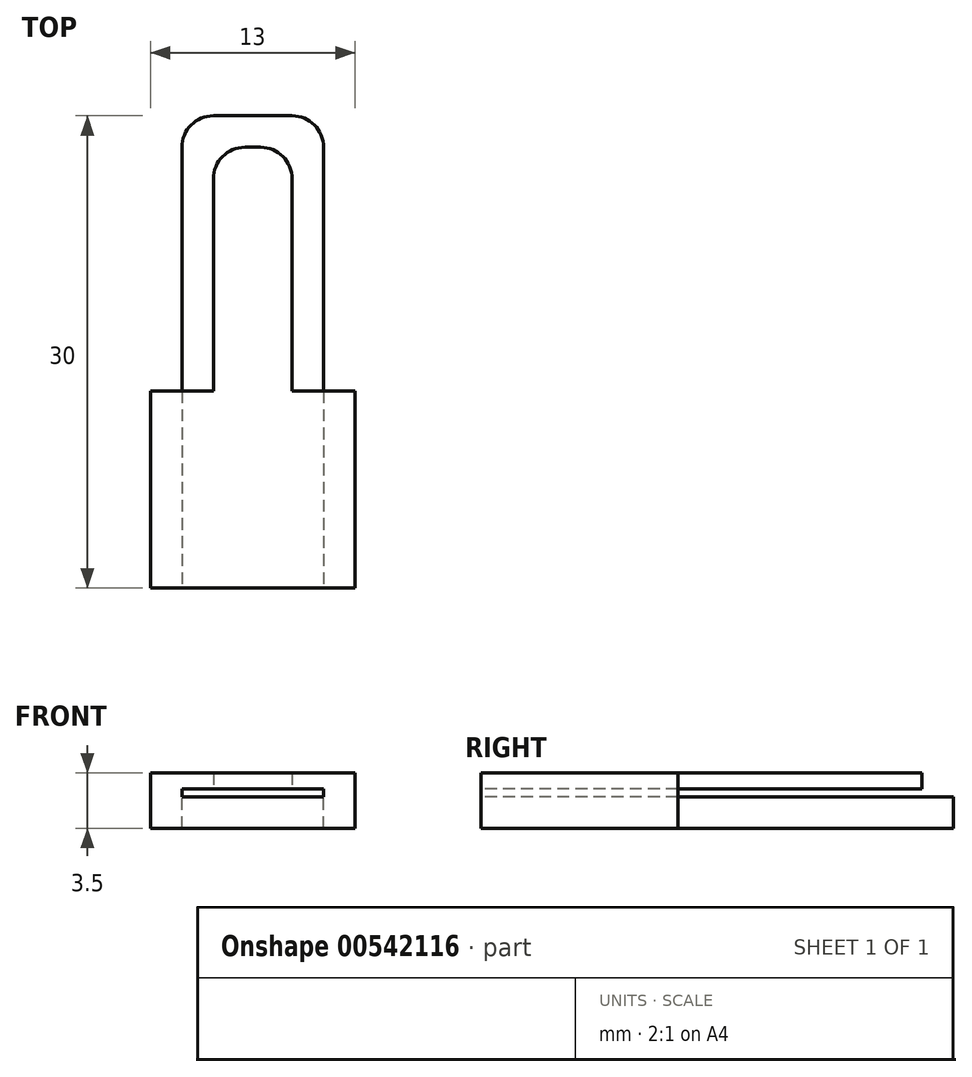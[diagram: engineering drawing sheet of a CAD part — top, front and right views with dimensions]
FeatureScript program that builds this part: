
annotation { "Feature Type Name" : "Feature", "Feature Type Description" : "" }
export const myFeature = defineFeature(function(context is Context, id is Id, definition is map)
    precondition{}
    {
        {
            var Q0;
            Q0=qCreatedBy(makeId("Top.planeOp"),FACE);
            var sketch = newSketch(context, id + "F0", { "sketchPlane" : qUnion([Q0])});
            skLineSegment(sketch, "E0.bottom", {"start": v(4.5, 15) * mm, "end": v(-4.5, 15) * mm});
            skLineSegment(sketch, "E0.top", {"start": v(4.5, -15) * mm, "end": v(-4.5, -15) * mm});
            skLineSegment(sketch, "E0.left", {"start": v(4.5, 15) * mm, "end": v(4.5, -15) * mm});
            skLineSegment(sketch, "E0.right", {"start": v(-4.5, 15) * mm, "end": v(-4.5, -15) * mm});
            skPoint(sketch, "E0.middle", {"position": v(0, 0) * mm});
            skLineSegment(sketch, "E1.bottom", {"start": v(-6.5, 12.5) * mm, "end": v(6.5, 12.5) * mm});
            skLineSegment(sketch, "E1.top", {"start": v(-6.5, -12.5) * mm, "end": v(6.5, -12.5) * mm});
            skLineSegment(sketch, "E1.left", {"start": v(-6.5, 12.5) * mm, "end": v(-6.5, -12.5) * mm});
            skLineSegment(sketch, "E1.right", {"start": v(6.5, 12.5) * mm, "end": v(6.5, -12.5) * mm});
            skLineSegment(sketch, "E2", {"start": v(-6.5, -2.5) * mm, "end": v(-4.5, -2.5) * mm});
            skLineSegment(sketch, "E3", {"start": v(4.5, -2.5) * mm, "end": v(6.5, -2.5) * mm});
            skSolve(sketch);
        }
        {
            var Q0;
            {var subQ0=sQuery(id+"F0.wireOp",EDGE,"E2");Q0=makeQuery(id+"F0.imprint","IMPRINT",FACE,{"disambiguationData":[TD([[makeQuery(id+"F0.imprint","IMPRINT",EDGE,{"derivedFrom":subQ0}),-1.0]])]});}
            var Q1;
            {var subQ0=sQuery(id+"F0.wireOp",EDGE,"E0.bottom");Q1=makeQuery(id+"F0.imprint","IMPRINT",FACE,{"disambiguationData":[TD([[makeQuery(id+"F0.imprint","IMPRINT",EDGE,{"derivedFrom":subQ0}),1.0]])]});}
            var Q2;
            {var subQ4=sQuery(id+"F0.wireOp",EDGE,"E0.left");var subQ5=makeQuery(id+"F0.imprint","INTERSECT",VERTEX,{"derivedFrom":[subQ4,sQuery(id+"F0.wireOp",EDGE,"E3")]});Q2=makeQuery(id+"F0.imprint","IMPRINT",FACE,{"disambiguationData":[TD([[makeQuery(id+"F0.imprint","IMPRINT",EDGE,{"disambiguationData":[TD([[subQ5,1.0]])],"derivedFrom":subQ4}),-1.0]])]});}
            var Q3;
            {var subQ0=sQuery(id+"F0.wireOp",EDGE,"E0.top");Q3=makeQuery(id+"F0.imprint","IMPRINT",FACE,{"disambiguationData":[TD([[makeQuery(id+"F0.imprint","IMPRINT",EDGE,{"derivedFrom":subQ0}),-1.0]])]});}
            var Q4;
            {var subQ0=sQuery(id+"F0.wireOp",EDGE,"E3");Q4=makeQuery(id+"F0.imprint","IMPRINT",FACE,{"disambiguationData":[TD([[makeQuery(id+"F0.imprint","IMPRINT",EDGE,{"derivedFrom":subQ0}),-1.0]])]});}
            var Q5;
            {var subQ0=sQuery(id+"F0.wireOp",EDGE,"E2");Q5=makeQuery(id+"F0.imprint","IMPRINT",FACE,{"disambiguationData":[TD([[makeQuery(id+"F0.imprint","IMPRINT",EDGE,{"derivedFrom":subQ0}),1.0]])]});}
            var Q6;
            {var subQ0=sQuery(id+"F0.wireOp",EDGE,"E3");Q6=makeQuery(id+"F0.imprint","IMPRINT",FACE,{"disambiguationData":[TD([[makeQuery(id+"F0.imprint","IMPRINT",EDGE,{"derivedFrom":subQ0}),1.0]])]});}
            extrude(context, id + "F1", {"entities" : qUnion([Q0, Q1, Q2, Q3, Q4, Q5, Q6]), "oppositeDirection" : true, "depth" : 2 * mm, "offsetDistance" : 25 * mm});
        }
        {
            var Q0;
            {var subQ0=sQuery(id+"F0.wireOp",EDGE,"E2");Q0=makeQuery(id+"F0.imprint","IMPRINT",FACE,{"disambiguationData":[TD([[makeQuery(id+"F0.imprint","IMPRINT",EDGE,{"derivedFrom":subQ0}),-1.0]])]});}
            var Q1;
            {var subQ0=sQuery(id+"F0.wireOp",EDGE,"E3");Q1=makeQuery(id+"F0.imprint","IMPRINT",FACE,{"disambiguationData":[TD([[makeQuery(id+"F0.imprint","IMPRINT",EDGE,{"derivedFrom":subQ0}),-1.0]])]});}
            extrude(context, id + "F2", {"entities" : qUnion([Q0, Q1]), "operationType" : NewBodyOperationType.ADD, "depth" : 0.5 * mm, "offsetDistance" : 25 * mm});
        }
        {
            var Q0;
            Q0=makeQuery(id+"F2.opExtrude","CAP_FACE",FACE,{"disambiguationData":[OSD([sQuery(id+"F0.wireOp",EDGE,"E0.right"),sQuery(id+"F0.wireOp",EDGE,"E1.top"),sQuery(id+"F0.wireOp",EDGE,"E1.left"),sQuery(id+"F0.wireOp",EDGE,"E2")])],"isStart":false});
            var sketch = newSketch(context, id + "F3", { "sketchPlane" : qUnion([Q0])});
            skLineSegment(sketch, "E4.bottom", {"start": v(-6.5, -12.5) * mm, "end": v(6.5, -12.5) * mm});
            skLineSegment(sketch, "E4.top", {"start": v(-6.5, -2.5) * mm, "end": v(6.5, -2.5) * mm});
            skLineSegment(sketch, "E4.left", {"start": v(-6.5, -12.5) * mm, "end": v(-6.5, -2.5) * mm});
            skLineSegment(sketch, "E4.right", {"start": v(6.5, -12.5) * mm, "end": v(6.5, -2.5) * mm});
            skLineSegment(sketch, "E5.bottom", {"start": v(-4.5, -2.5) * mm, "end": v(4.5, -2.5) * mm});
            skLineSegment(sketch, "E6.bottom", {"start": v(-2.5, 13) * mm, "end": v(2.5, 13) * mm});
            skLineSegment(sketch, "E6.top", {"start": v(-2.5, -2.5) * mm, "end": v(2.5, -2.5) * mm});
            skLineSegment(sketch, "E6.left", {"start": v(-2.5, 13) * mm, "end": v(-2.5, -2.5) * mm});
            skLineSegment(sketch, "E6.right", {"start": v(2.5, 13) * mm, "end": v(2.5, -2.5) * mm});
            skPoint(sketch, "E6.middle", {"position": v(0, 5.25) * mm});
            skPoint(sketch, "E6.middle.positionSnap0", {"position": v(-4.5, 5.25) * mm});
            skPoint(sketch, "E6.middle.positionSnap1", {"position": v(0, -2.5) * mm});
            skPoint(sketch, "E6.centerSnap0", {"position": v(-4.5, 5.25) * mm});
            skPoint(sketch, "E6.centerSnap1", {"position": v(0, -2.5) * mm});
            skSolve(sketch);
        }
        {
            var Q0;
            {var subQ0=sQuery(id+"F3.wireOp",EDGE,"E4.left");Q0=makeQuery(id+"F3.imprint","IMPRINT",FACE,{"disambiguationData":[TD([[makeQuery(id+"F3.imprint","IMPRINT",EDGE,{"derivedFrom":subQ0}),1.0]])]});}
            var Q1;
            {var subQ0=sQuery(id+"F3.wireOp",EDGE,"E4.right");Q1=makeQuery(id+"F3.imprint","IMPRINT",FACE,{"disambiguationData":[TD([[makeQuery(id+"F3.imprint","IMPRINT",EDGE,{"derivedFrom":subQ0}),1.0]])]});}
            var Q2;
            Q2=makeQuery(id+"F3.imprint","IMPRINT",FACE,{"disambiguationData":[TD([[makeQuery(id+"F3.imprint","IMPRINT",EDGE,{"derivedFrom":sQuery(id+"F3.wireOp",EDGE,"E5.bottom")}),1.0]])]});
            var Q3;
            Q3=makeQuery(id+"F3.imprint","IMPRINT",FACE,{"disambiguationData":[TD([[makeQuery(id+"F3.imprint","IMPRINT",EDGE,{"derivedFrom":sQuery(id+"F3.wireOp",EDGE,"E6.bottom")}),-1.0]])]});
            extrude(context, id + "F4", {"entities" : qUnion([Q0, Q1, Q2, Q3]), "operationType" : NewBodyOperationType.ADD, "depth" : 1 * mm, "offsetDistance" : 25 * mm});
        }
        {
            var Q0;
            Q0=makeQuery(id+"F1.opExtrude","SWEPT_EDGE",EDGE,{"disambiguationData":[OSD([sQuery(id+"F0.wireOp",EDGE,"E0.bottom"),sQuery(id+"F0.wireOp",EDGE,"E0.right")])]});
            var Q1;
            Q1=makeQuery(id+"F1.opExtrude","SWEPT_EDGE",EDGE,{"disambiguationData":[OSD([sQuery(id+"F0.wireOp",EDGE,"E0.bottom"),sQuery(id+"F0.wireOp",EDGE,"E0.left")])]});
            var Q2;
            Q2=makeQuery(id+"F4.opExtrude","SWEPT_EDGE",EDGE,{"disambiguationData":[OSD([sQuery(id+"F3.wireOp",EDGE,"E5.top"),sQuery(id+"F3.wireOp",EDGE,"E5.left")])]});
            var Q3;
            Q3=makeQuery(id+"F4.opExtrude","SWEPT_EDGE",EDGE,{"disambiguationData":[OSD([sQuery(id+"F3.wireOp",EDGE,"E5.top"),sQuery(id+"F3.wireOp",EDGE,"E5.right")])]});
            var Q4;
            Q4=makeQuery(id+"F4.opExtrude","SWEPT_EDGE",EDGE,{"disambiguationData":[OSD([sQuery(id+"F3.wireOp",EDGE,"E6.bottom"),sQuery(id+"F3.wireOp",EDGE,"E6.left")])]});
            var Q5;
            Q5=makeQuery(id+"F4.opExtrude","SWEPT_EDGE",EDGE,{"disambiguationData":[OSD([sQuery(id+"F3.wireOp",EDGE,"E6.bottom"),sQuery(id+"F3.wireOp",EDGE,"E6.right")])]});
            fillet(context, id + "F5", {"entities" : qUnion([Q0, Q1, Q2, Q3, Q4, Q5]), "radius" : 2 * mm, "tangentPropagation" : true, "allowEdgeOverflow" : false});
        }
        {
            var Q0;
            {var subQ0=sQuery(id+"F0.wireOp",EDGE,"E2");Q0=makeQuery(id+"F0.imprint","IMPRINT",FACE,{"disambiguationData":[TD([[makeQuery(id+"F0.imprint","IMPRINT",EDGE,{"derivedFrom":subQ0}),1.0]])]});}
            var Q1;
            {var subQ0=sQuery(id+"F0.wireOp",EDGE,"E3");Q1=makeQuery(id+"F0.imprint","IMPRINT",FACE,{"disambiguationData":[TD([[makeQuery(id+"F0.imprint","IMPRINT",EDGE,{"derivedFrom":subQ0}),1.0]])]});}
            extrude(context, id + "F6", {"entities" : qUnion([Q0, Q1]), "operationType" : NewBodyOperationType.REMOVE, "oppositeDirection" : true, "depth" : 25 * mm, "offsetDistance" : 25 * mm});
        }
        {
            var Q0;
            {var subQ0=sQuery(id+"F0.wireOp",EDGE,"E1.top");var subQ1=makeQuery(id+"F0.imprint","IMPRINT",EDGE,{"disambiguationData":[TD([[makeQuery(id+"F0.imprint","INTERSECT",VERTEX,{"derivedFrom":[subQ0,sQuery(id+"F0.wireOp",EDGE,"E1.right")]}),1.0]])],"derivedFrom":subQ0});var subQ2=makeQuery(id+"F0.imprint","IMPRINT",EDGE,{"disambiguationData":[TD([[makeQuery(id+"F0.imprint","INTERSECT",VERTEX,{"derivedFrom":[subQ0,sQuery(id+"F0.wireOp",EDGE,"E1.left")]}),-1.0]])],"derivedFrom":subQ0});Q0=makeQuery(id+"F4.boolean.opBoolean","MERGE",FACE,{"derivedFrom":[makeQuery(id+"F2.boolean.opBoolean","MERGE",FACE,{"derivedFrom":[makeQuery(id+"F1.opExtrude","SWEPT_FACE",FACE,{"disambiguationData":[OSD([subQ0]),TDD([subQ2])]}),makeQuery(id+"F2.opExtrude","SWEPT_FACE",FACE,{"disambiguationData":[OSD([subQ0]),TDD([subQ2])]})]}),makeQuery(id+"F2.boolean.opBoolean","MERGE",FACE,{"derivedFrom":[makeQuery(id+"F1.opExtrude","SWEPT_FACE",FACE,{"disambiguationData":[OSD([subQ0]),TDD([subQ1])]}),makeQuery(id+"F2.opExtrude","SWEPT_FACE",FACE,{"disambiguationData":[OSD([subQ0]),TDD([subQ1])]})]}),makeQuery(id+"F4.opExtrude","SWEPT_FACE",FACE,{"disambiguationData":[OSD([sQuery(id+"F3.wireOp",EDGE,"E4.bottom")])]})]});}
            var Q1;
            Q1=makeQuery(id+"F1.opExtrude","SWEPT_FACE",FACE,{"disambiguationData":[OSD([sQuery(id+"F0.wireOp",EDGE,"E0.top")])]});
            extrude(context, id + "F7", {"entities" : qUnion([Q0]), "operationType" : NewBodyOperationType.ADD, "endBound" : BoundingType.UP_TO_SURFACE, "depth" : 25 * mm, "endBoundEntityFace" : qUnion([Q1]), "offsetDistance" : 25 * mm});
        }
    });
